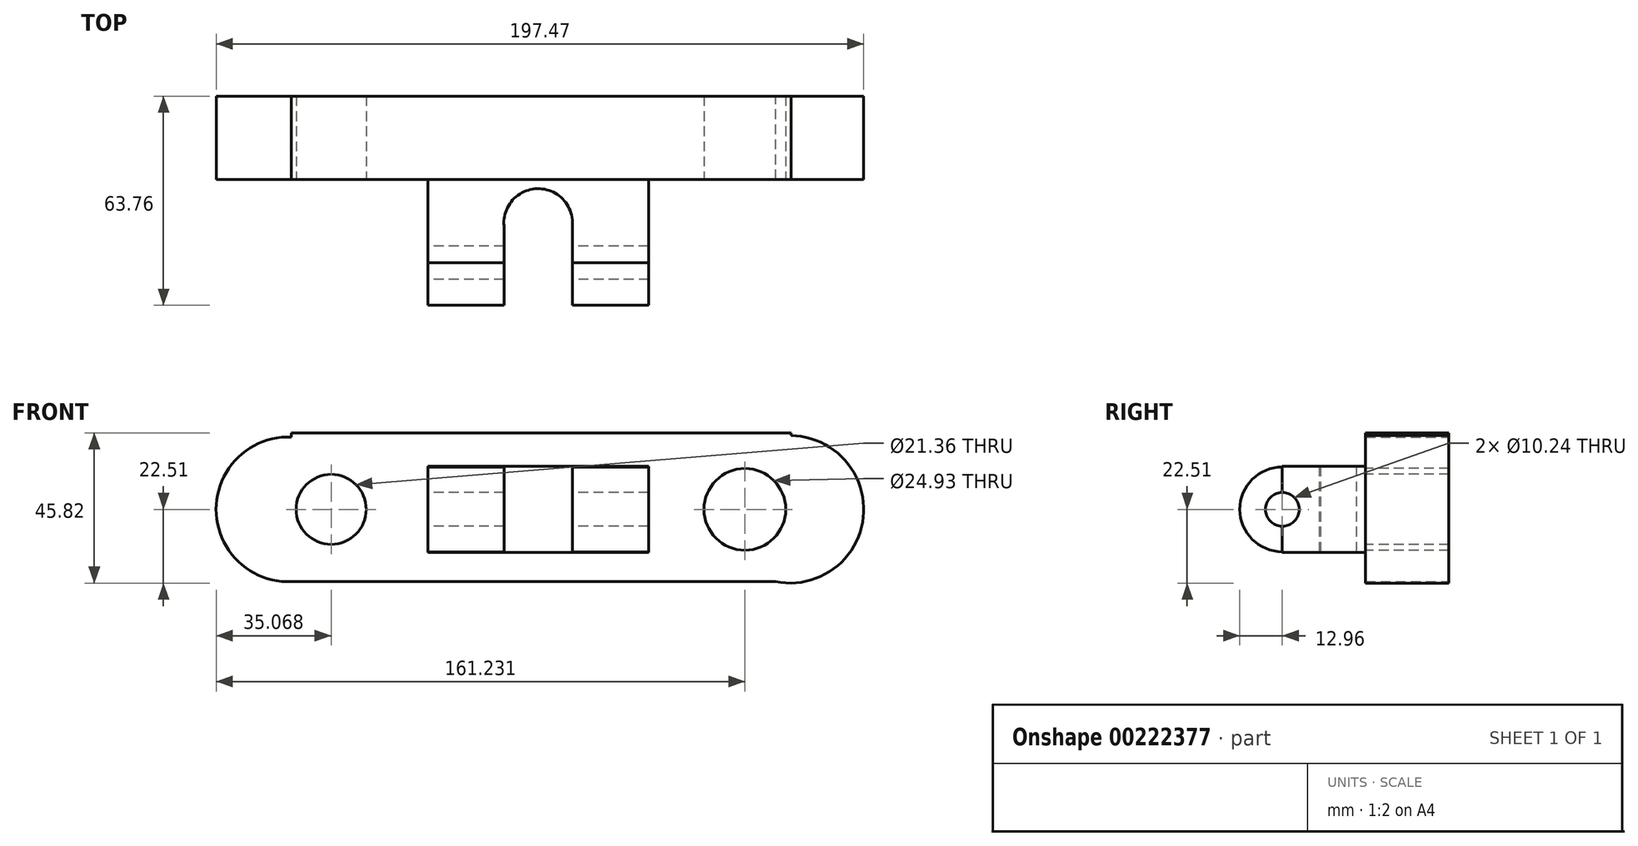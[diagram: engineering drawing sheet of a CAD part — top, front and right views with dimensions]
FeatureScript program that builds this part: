
annotation { "Feature Type Name" : "Feature", "Feature Type Description" : "" }
export const myFeature = defineFeature(function(context is Context, id is Id, definition is map)
    precondition{}
    {
        {
            var Q0;
            Q0=qCreatedBy(makeId("Front.planeOp"),FACE);
            var sketch = newSketch(context, id + "F13", { "sketchPlane" : qUnion([Q0])});
            skLineSegment(sketch, "E0.bottom", {"start": v(77.08, 23.3) * mm, "end": v(-75.23, 23.3) * mm});
            skLineSegment(sketch, "E0.top", {"start": v(77.08, -22.08) * mm, "end": v(-75.23, -22.08) * mm});
            skLineSegment(sketch, "E0.left", {"start": v(77.08, 23.3) * mm, "end": v(77.08, -22.08) * mm});
            skLineSegment(sketch, "E0.right", {"start": v(-75.23, 23.3) * mm, "end": v(-75.23, -22.08) * mm});
            skPoint(sketch, "E0.middle", {"position": v(0.92, 0.61) * mm});
            skSolve(sketch);
        }
        {
            var Q0;
            Q0=makeQuery(id+"F13.imprint","IMPRINT",FACE,{"disambiguationData":[TD([[makeQuery(id+"F13.imprint","IMPRINT",EDGE,{"derivedFrom":sQuery(id+"F13.wireOp",EDGE,"E0.bottom")}),1.0]])]});
            var sketch = newSketch(context, id + "F0", { "sketchPlane" : qUnion([Q0])});
            skCircle(sketch, "E1", {"center": v(76.76, 0) * mm, "radius": 22.5 * mm});
            skSolve(sketch);
        }
        {
            var Q0;
            Q0=makeQuery(id+"F13.imprint","IMPRINT",FACE,{"disambiguationData":[TD([[makeQuery(id+"F13.imprint","IMPRINT",EDGE,{"derivedFrom":sQuery(id+"F13.wireOp",EDGE,"E0.bottom")}),1.0]])]});
            var sketch = newSketch(context, id + "F14", { "sketchPlane" : qUnion([Q0])});
            skCircle(sketch, "E2", {"center": v(-76.12, 0) * mm, "radius": 22.08 * mm});
            skSolve(sketch);
        }
        {
            var Q0;
            Q0=makeQuery(id+"F13.imprint","IMPRINT",FACE,{"disambiguationData":[TD([[makeQuery(id+"F13.imprint","IMPRINT",EDGE,{"derivedFrom":sQuery(id+"F13.wireOp",EDGE,"E0.bottom")}),1.0]])]});
            extrude(context, id + "F1", {"entities" : qUnion([Q0]), "depth" : 25.4 * mm});
        }
        {
            var Q0;
            {var subQ0=sQuery(id+"F14.wireOp",EDGE,"E2");var subQ1=makeQuery(id+"F13.imprint","IMPRINT",EDGE,{"derivedFrom":sQuery(id+"F13.wireOp",EDGE,"E0.right")});var subQ2=makeQuery(id+"F14.imprint","INTERSECT",VERTEX,{"disambiguationData":[OD(0.0)],"derivedFrom":[subQ1,subQ0]});Q0=makeQuery(id+"F14.imprint","IMPRINT",FACE,{"disambiguationData":[TD([[makeQuery(id+"F14.imprint","IMPRINT",EDGE,{"disambiguationData":[TD([[subQ2,-1.0]])],"derivedFrom":subQ0}),1.0]])]});}
            var Q1;
            {var subQ0=sQuery(id+"F0.wireOp",EDGE,"E1");var subQ1=makeQuery(id+"F13.imprint","IMPRINT",EDGE,{"derivedFrom":sQuery(id+"F13.wireOp",EDGE,"E0.top")});var subQ2=makeQuery(id+"F0.imprint","INTERSECT",VERTEX,{"derivedFrom":[subQ1,subQ0]});Q1=makeQuery(id+"F0.imprint","IMPRINT",FACE,{"disambiguationData":[TD([[makeQuery(id+"F0.imprint","IMPRINT",EDGE,{"disambiguationData":[TD([[subQ2,-1.0]])],"derivedFrom":subQ0}),1.0]])]});}
            extrude(context, id + "F2", {"entities" : qUnion([Q0, Q1]), "operationType" : NewBodyOperationType.ADD, "depth" : 25.4 * mm});
        }
        {
            var Q0;
            {var subQ0=sQuery(id+"F13.wireOp",EDGE,"E0.right");var subQ1=sQuery(id+"F13.wireOp",EDGE,"E0.left");var subQ2=sQuery(id+"F13.wireOp",EDGE,"E0.top");Q0=makeQuery(id+"F2.boolean.opBoolean","MERGE",FACE,{"derivedFrom":[makeQuery(id+"F1.opExtrude","CAP_FACE",FACE,{"disambiguationData":[OSD([sQuery(id+"F13.wireOp",EDGE,"E0.bottom"),subQ2,subQ1,subQ0])],"isStart":false}),makeQuery(id+"F2.opExtrude","CAP_FACE",FACE,{"disambiguationData":[OSD([subQ2,subQ1,sQuery(id+"F0.wireOp",EDGE,"E1")])],"isStart":false}),makeQuery(id+"F2.opExtrude","CAP_FACE",FACE,{"disambiguationData":[OSD([subQ0,sQuery(id+"F14.wireOp",EDGE,"E2")])],"isStart":false})]});}
            var sketch = newSketch(context, id + "F3", { "sketchPlane" : qUnion([Q0])});
            skLineSegment(sketch, "E3.bottom", {"start": v(33.68, -13.1) * mm, "end": v(-33.68, -13.1) * mm});
            skLineSegment(sketch, "E3.top", {"start": v(33.68, 13.1) * mm, "end": v(-33.68, 13.1) * mm});
            skLineSegment(sketch, "E3.left", {"start": v(33.68, -13.1) * mm, "end": v(33.68, 13.1) * mm});
            skLineSegment(sketch, "E3.right", {"start": v(-33.68, -13.1) * mm, "end": v(-33.68, 13.1) * mm});
            skPoint(sketch, "E3.middle", {"position": v(0, 0) * mm});
            skSolve(sketch);
        }
        {
            var Q0;
            {var subQ0=sQuery(id+"F13.wireOp",EDGE,"E0.right");var subQ1=sQuery(id+"F13.wireOp",EDGE,"E0.left");var subQ2=sQuery(id+"F13.wireOp",EDGE,"E0.top");Q0=makeQuery(id+"F2.boolean.opBoolean","MERGE",FACE,{"derivedFrom":[makeQuery(id+"F1.opExtrude","CAP_FACE",FACE,{"disambiguationData":[OSD([sQuery(id+"F13.wireOp",EDGE,"E0.bottom"),subQ2,subQ1,subQ0])],"isStart":false}),makeQuery(id+"F2.opExtrude","CAP_FACE",FACE,{"disambiguationData":[OSD([subQ2,subQ1,sQuery(id+"F0.wireOp",EDGE,"E1")])],"isStart":false}),makeQuery(id+"F2.opExtrude","CAP_FACE",FACE,{"disambiguationData":[OSD([subQ0,sQuery(id+"F14.wireOp",EDGE,"E2")])],"isStart":false})]});}
            var sketch = newSketch(context, id + "F4", { "sketchPlane" : qUnion([Q0])});
            skCircle(sketch, "E4", {"center": v(-63.13, 0) * mm, "radius": 10.68 * mm});
            skSolve(sketch);
        }
        {
            var Q0;
            Q0=makeQuery(id+"F4.imprint","IMPRINT",FACE,{"disambiguationData":[TD([[makeQuery(id+"F4.imprint","IMPRINT",EDGE,{"derivedFrom":sQuery(id+"F4.wireOp",EDGE,"E4")}),1.0]])]});
            extrude(context, id + "F5", {"entities" : qUnion([Q0]), "operationType" : NewBodyOperationType.REMOVE, "endBound" : BoundingType.THROUGH_ALL, "oppositeDirection" : true, "depth" : 25.4 * mm});
        }
        {
            var Q0;
            {var subQ0=sQuery(id+"F13.wireOp",EDGE,"E0.right");var subQ1=sQuery(id+"F13.wireOp",EDGE,"E0.left");var subQ2=sQuery(id+"F13.wireOp",EDGE,"E0.top");Q0=makeQuery(id+"F2.boolean.opBoolean","MERGE",FACE,{"derivedFrom":[makeQuery(id+"F1.opExtrude","CAP_FACE",FACE,{"disambiguationData":[OSD([sQuery(id+"F13.wireOp",EDGE,"E0.bottom"),subQ2,subQ1,subQ0])],"isStart":false}),makeQuery(id+"F2.opExtrude","CAP_FACE",FACE,{"disambiguationData":[OSD([subQ2,subQ1,sQuery(id+"F0.wireOp",EDGE,"E1")])],"isStart":false}),makeQuery(id+"F2.opExtrude","CAP_FACE",FACE,{"disambiguationData":[OSD([subQ0,sQuery(id+"F14.wireOp",EDGE,"E2")])],"isStart":false})]});}
            var sketch = newSketch(context, id + "F6", { "sketchPlane" : qUnion([Q0])});
            skCircle(sketch, "E5", {"center": v(63.03, 0) * mm, "radius": 12.47 * mm});
            skSolve(sketch);
        }
        {
            var Q0;
            Q0=makeQuery(id+"F6.imprint","IMPRINT",FACE,{"disambiguationData":[TD([[makeQuery(id+"F6.imprint","IMPRINT",EDGE,{"derivedFrom":sQuery(id+"F6.wireOp",EDGE,"E5")}),1.0]])]});
            extrude(context, id + "F15", {"entities" : qUnion([Q0]), "operationType" : NewBodyOperationType.REMOVE, "endBound" : BoundingType.THROUGH_ALL, "oppositeDirection" : true, "depth" : 25.4 * mm});
        }
        {
            var Q0;
            Q0=makeQuery(id+"F3.imprint","IMPRINT",FACE,{"disambiguationData":[TD([[makeQuery(id+"F3.imprint","IMPRINT",EDGE,{"derivedFrom":sQuery(id+"F3.wireOp",EDGE,"E3.bottom")}),-1.0]])]});
            extrude(context, id + "F16", {"entities" : qUnion([Q0]), "operationType" : NewBodyOperationType.ADD, "depth" : 25.4 * mm});
        }
        {
            var Q0;
            Q0=makeQuery(id+"F16.opExtrude","SWEPT_FACE",FACE,{"disambiguationData":[OSD([sQuery(id+"F3.wireOp",EDGE,"E3.right")])]});
            var sketch = newSketch(context, id + "F7", { "sketchPlane" : qUnion([Q0])});
            skCircle(sketch, "E6", {"center": v(50.8, 0) * mm, "radius": 12.96 * mm});
            skSolve(sketch);
        }
        {
            var Q0;
            {var subQ0=sQuery(id+"F7.wireOp",EDGE,"E6");var subQ1=makeQuery(id+"F16.opExtrude","CAP_EDGE",EDGE,{"disambiguationData":[OSD([sQuery(id+"F3.wireOp",EDGE,"E3.right")])],"isStart":false});var subQ2=makeQuery(id+"F7.imprint","INTERSECT",VERTEX,{"disambiguationData":[OD(0.0)],"derivedFrom":[subQ1,subQ0]});Q0=makeQuery(id+"F7.imprint","IMPRINT",FACE,{"disambiguationData":[TD([[makeQuery(id+"F7.imprint","IMPRINT",EDGE,{"disambiguationData":[TD([[subQ2,-1.0]])],"derivedFrom":subQ0}),1.0]])]});}
            extrude(context, id + "F17", {"entities" : qUnion([Q0]), "operationType" : NewBodyOperationType.ADD, "oppositeDirection" : true, "depth" : 67.4 * mm});
        }
        {
            var Q0;
            Q0=makeQuery(id+"F16.opExtrude","SWEPT_FACE",FACE,{"disambiguationData":[OSD([sQuery(id+"F3.wireOp",EDGE,"E3.bottom")])]});
            var sketch = newSketch(context, id + "F8", { "sketchPlane" : qUnion([Q0])});
            skCircle(sketch, "E7", {"center": v(0, 38.68) * mm, "radius": 10.46 * mm});
            skSolve(sketch);
        }
        {
            var Q0;
            Q0=makeQuery(id+"F8.imprint","IMPRINT",FACE,{"disambiguationData":[TD([[makeQuery(id+"F8.imprint","IMPRINT",EDGE,{"derivedFrom":sQuery(id+"F8.wireOp",EDGE,"E7")}),1.0]])]});
            var sketch = newSketch(context, id + "F9", { "sketchPlane" : qUnion([Q0])});
            skLineSegment(sketch, "E8.bottom", {"start": v(-10.42, 39.13) * mm, "end": v(10.45, 39.13) * mm});
            skLineSegment(sketch, "E8.top", {"start": v(-10.42, 65.86) * mm, "end": v(10.45, 65.86) * mm});
            skLineSegment(sketch, "E8.left", {"start": v(-10.42, 39.13) * mm, "end": v(-10.42, 65.86) * mm});
            skLineSegment(sketch, "E8.right", {"start": v(10.45, 39.13) * mm, "end": v(10.45, 65.86) * mm});
            skSolve(sketch);
        }
        {
            var Q0;
            Q0=makeQuery(id+"F8.imprint","IMPRINT",FACE,{"disambiguationData":[TD([[makeQuery(id+"F8.imprint","IMPRINT",EDGE,{"derivedFrom":sQuery(id+"F8.wireOp",EDGE,"E7")}),1.0]])]});
            var Q1;
            {var subQ2=sQuery(id+"F9.wireOp",EDGE,"E8.top");Q1=makeQuery(id+"F9.imprint","IMPRINT",FACE,{"disambiguationData":[TD([[makeQuery(id+"F9.imprint","IMPRINT",EDGE,{"derivedFrom":subQ2}),-1.0]])]});}
            extrude(context, id + "F10", {"entities" : qUnion([Q0, Q1]), "operationType" : NewBodyOperationType.REMOVE, "endBound" : BoundingType.THROUGH_ALL, "oppositeDirection" : true, "depth" : 37.95 * mm});
        }
        {
            var Q0;
            {var subQ0=sQuery(id+"F3.wireOp",EDGE,"E3.right");Q0=makeQuery(id+"F17.boolean.opBoolean","MERGE",FACE,{"derivedFrom":[makeQuery(id+"F16.opExtrude","SWEPT_FACE",FACE,{"disambiguationData":[OSD([subQ0])]}),makeQuery(id+"F17.opExtrude","CAP_FACE",FACE,{"disambiguationData":[OSD([subQ0,sQuery(id+"F7.wireOp",EDGE,"E6")])],"isStart":true})]});}
            var sketch = newSketch(context, id + "F11", { "sketchPlane" : qUnion([Q0])});
            skCircle(sketch, "E9", {"center": v(50.8, 0) * mm, "radius": 5.12 * mm});
            skSolve(sketch);
        }
        {
            var Q0;
            Q0=makeQuery(id+"F11.imprint","IMPRINT",FACE,{"disambiguationData":[TD([[makeQuery(id+"F11.imprint","IMPRINT",EDGE,{"derivedFrom":sQuery(id+"F11.wireOp",EDGE,"E9")}),1.0]])]});
            extrude(context, id + "F12", {"entities" : qUnion([Q0]), "operationType" : NewBodyOperationType.REMOVE, "endBound" : BoundingType.THROUGH_ALL, "oppositeDirection" : true, "depth" : 25.4 * mm});
        }
    });
